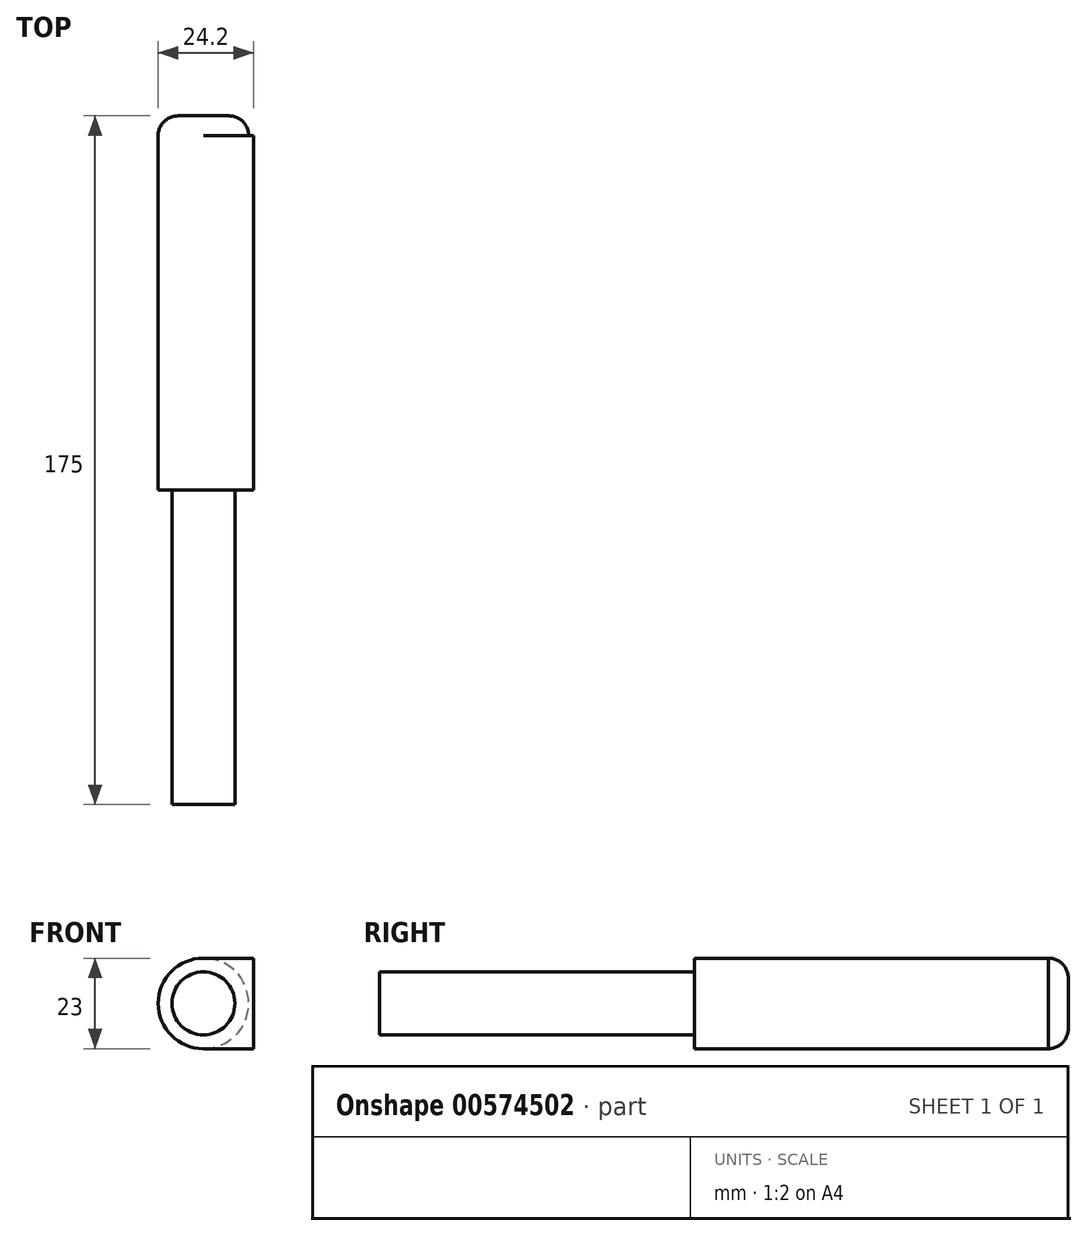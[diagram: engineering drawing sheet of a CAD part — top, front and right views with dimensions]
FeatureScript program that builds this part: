
annotation { "Feature Type Name" : "Feature", "Feature Type Description" : "" }
export const myFeature = defineFeature(function(context is Context, id is Id, definition is map)
    precondition{}
    {
        {
            var Q0;
            Q0=qCreatedBy(makeId("Front.planeOp"),FACE);
            var sketch = newSketch(context, id + "F0", { "sketchPlane" : qUnion([Q0])});
            skCircle(sketch, "E0", {"center": v(0, 0) * mm, "radius": 11.5 * mm});
            skSolve(sketch);
        }
        {
            var Q0;
            Q0=qCreatedBy(makeId("Front.planeOp"),FACE);
            var sketch = newSketch(context, id + "F1", { "sketchPlane" : qUnion([Q0])});
            skCircle(sketch, "E1", {"center": v(0, 0) * mm, "radius": 8 * mm});
            skSolve(sketch);
        }
        {
            var Q0;
            Q0=makeQuery(id+"F0.imprint","IMPRINT",FACE,{"disambiguationData":[TD([[makeQuery(id+"F0.imprint","IMPRINT",EDGE,{"derivedFrom":sQuery(id+"F0.wireOp",EDGE,"E0")}),1.0]])]});
            extrude(context, id + "F2", {"entities" : qUnion([Q0]), "oppositeDirection" : true, "depth" : 95 * mm, "offsetDistance" : 25 * mm});
        }
        {
            var Q0;
            Q0=makeQuery(id+"F1.imprint","IMPRINT",FACE,{"disambiguationData":[TD([[makeQuery(id+"F1.imprint","IMPRINT",EDGE,{"derivedFrom":sQuery(id+"F1.wireOp",EDGE,"E1")}),1.0]])]});
            extrude(context, id + "F3", {"entities" : qUnion([Q0]), "operationType" : NewBodyOperationType.ADD, "depth" : 80 * mm, "offsetDistance" : 25 * mm});
        }
        {
            var Q0;
            Q0=makeQuery(id+"F2.opExtrude","CAP_EDGE",EDGE,{"disambiguationData":[OSD([sQuery(id+"F0.wireOp",EDGE,"E0")])],"isStart":false});
            fillet(context, id + "F4", {"entities" : qUnion([Q0]), "radius" : 5 * mm, "tangentPropagation" : true, "allowEdgeOverflow" : false});
        }
        {
            var Q0;
            Q0=qCreatedBy(makeId("Right.planeOp"),FACE);
            var sketch = newSketch(context, id + "F5", { "sketchPlane" : qUnion([Q0])});
            skLineSegment(sketch, "E2", {"start": v(0, 11.5) * mm, "end": v(90, 11.5) * mm});
            skLineSegment(sketch, "E3", {"start": v(90, -11.5) * mm, "end": v(0, -11.5) * mm});
            skLineSegment(sketch, "E4.top", {"start": v(0, -11.5) * mm, "end": v(90, -11.5) * mm});
            skLineSegment(sketch, "E4.left", {"start": v(0, 11.5) * mm, "end": v(0, -11.5) * mm});
            skLineSegment(sketch, "E4.right", {"start": v(90, 11.5) * mm, "end": v(90, -11.5) * mm});
            skSolve(sketch);
        }
        {
            var Q0;
            Q0 = qSketchRegion(id + "F5", true);
            extrude(context, id + "F6", {"entities" : qUnion([Q0]), "operationType" : NewBodyOperationType.ADD, "depth" : 12.7 * mm, "offsetDistance" : 25 * mm});
        }
    });
